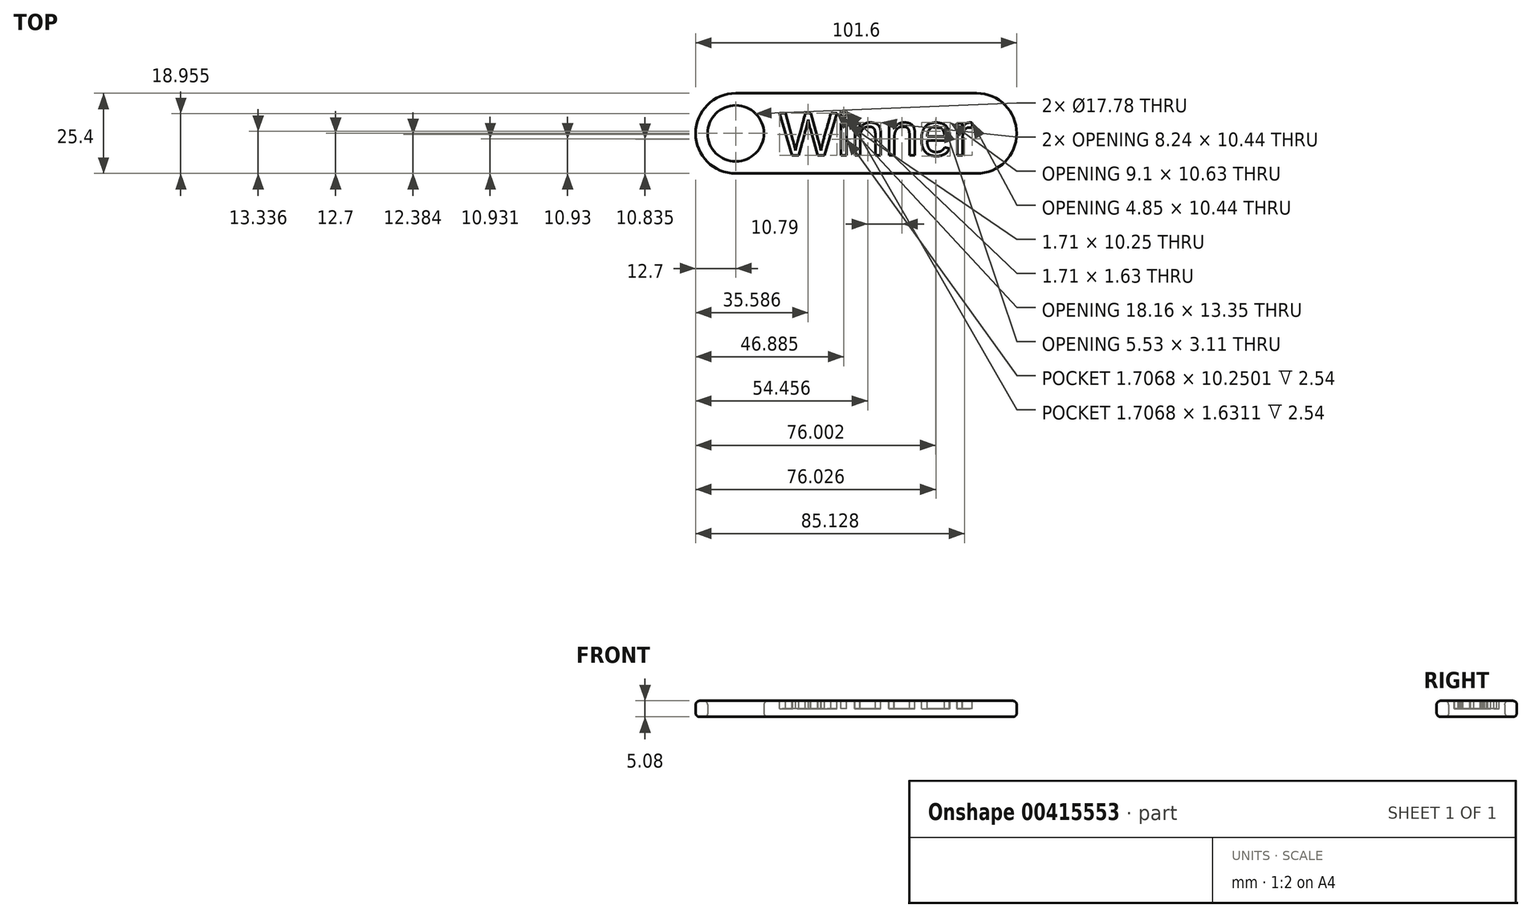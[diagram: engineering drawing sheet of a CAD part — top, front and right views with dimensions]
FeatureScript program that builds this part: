
annotation { "Feature Type Name" : "Feature", "Feature Type Description" : "" }
export const myFeature = defineFeature(function(context is Context, id is Id, definition is map)
    precondition{}
    {
        {
            var Q0;
            Q0=qCreatedBy(makeId("Top.planeOp"),FACE);
            var sketch = newSketch(context, id + "F0", { "sketchPlane" : qUnion([Q0])});
            skLineSegment(sketch, "E0.bottom", {"start": v(38.1, -12.7) * mm, "end": v(-38.1, -12.7) * mm});
            skLineSegment(sketch, "E0.top", {"start": v(38.1, 12.7) * mm, "end": v(-38.1, 12.7) * mm});
            skPoint(sketch, "E0.middle", {"position": v(0, 0) * mm});
            skArc(sketch, "E1", {"start": v(38.1, -12.7) * mm, "mid": v(50.8, 0) * mm, "end": v(38.1, 12.7) * mm});
            skArc(sketch, "E2", {"start": v(-38.1, 12.7) * mm, "mid": v(-50.8, 0) * mm, "end": v(-38.1, -12.7) * mm});
            skCircle(sketch, "E3", {"center": v(-38.1, 0) * mm, "radius": 8.9 * mm});
            skSolve(sketch);
        }
        {
            var Q0;
            Q0=makeQuery(id+"F0.imprint","IMPRINT",FACE,{"disambiguationData":[TD([[makeQuery(id+"F0.imprint","IMPRINT",EDGE,{"derivedFrom":sQuery(id+"F0.wireOp",EDGE,"E0.bottom")}),-1.0]])]});
            extrude(context, id + "F1", {"entities" : qUnion([Q0]), "depth" : 5.08 * mm});
        }
        {
            var Q0;
            Q0=makeQuery(id+"F1.opExtrude","CAP_FACE",FACE,{"disambiguationData":[OSD([sQuery(id+"F0.wireOp",EDGE,"E0.bottom"),sQuery(id+"F0.wireOp",EDGE,"E0.top"),sQuery(id+"F0.wireOp",EDGE,"E1"),sQuery(id+"F0.wireOp",EDGE,"E2"),sQuery(id+"F0.wireOp",EDGE,"E3")])],"isStart":false});
            var sketch = newSketch(context, id + "F2", { "sketchPlane" : qUnion([Q0])});
            skText(sketch, "E4", { "text": "Winner", "fontName": "Arimo-Regular.ttf"});
            const initialGuessF2  = {"E4": [-0.02438, -0.00699, 1, 0, 0.01397]};
            skSetInitialGuess(sketch, initialGuessF2);
            skSolve(sketch);
        }
        {
            var Q0;
            Q0=qSketchRegion(id+"F2",true);
            extrude(context, id + "F3", {"entities" : qUnion([Q0]), "operationType" : NewBodyOperationType.REMOVE, "oppositeDirection" : true, "depth" : 2.54 * mm});
        }
        {
            var Q0;
            Q0=makeQuery(id+"F1.opExtrude","CAP_EDGE",EDGE,{"disambiguationData":[OSD([sQuery(id+"F0.wireOp",EDGE,"E2")])],"isStart":false});
            var Q1;
            Q1=makeQuery(id+"F1.opExtrude","CAP_FACE",FACE,{"disambiguationData":[OSD([sQuery(id+"F0.wireOp",EDGE,"E0.bottom"),sQuery(id+"F0.wireOp",EDGE,"E0.top"),sQuery(id+"F0.wireOp",EDGE,"E1"),sQuery(id+"F0.wireOp",EDGE,"E2"),sQuery(id+"F0.wireOp",EDGE,"E3")])],"isStart":true});
            var Q2;
            Q2=makeQuery(id+"F1.opExtrude","CAP_EDGE",EDGE,{"disambiguationData":[OSD([sQuery(id+"F0.wireOp",EDGE,"E3")])],"isStart":false});
            fillet(context, id + "F4", {"entities" : qUnion([Q0, Q1, Q2]), "radius" : 1.27 * mm, "tangentPropagation" : true, "allowEdgeOverflow" : false});
        }
    });
